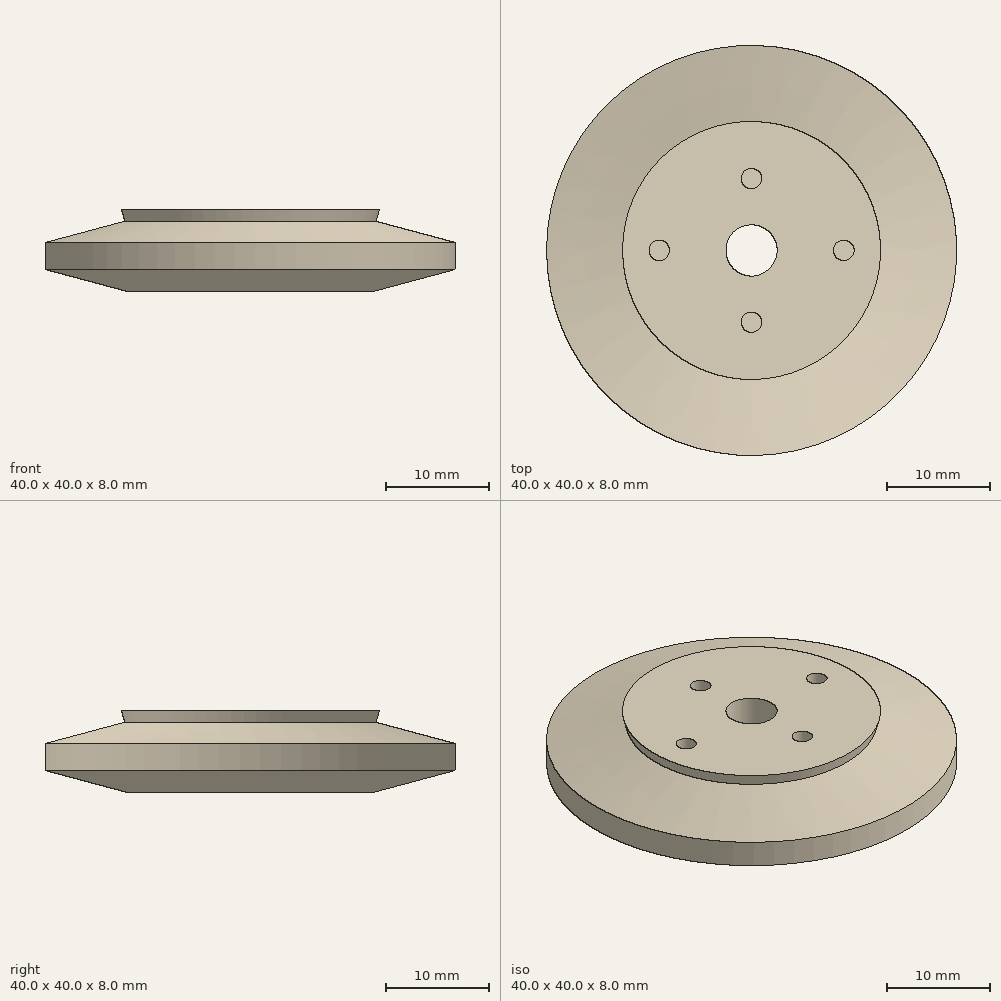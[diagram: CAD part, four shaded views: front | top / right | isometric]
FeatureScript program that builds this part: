
annotation { "Feature Type Name" : "Feature", "Feature Type Description" : "" }
export const myFeature = defineFeature(function(context is Context, id is Id, definition is map)
    precondition{}
    {
        {
            var Q0;
            Q0=qCreatedBy(makeId("Front.planeOp"),FACE);
            var sketch = newSketch(context, id + "F0", { "sketchPlane" : qUnion([Q0])});
            skLineSegment(sketch, "E0", {"start": v(0, 0) * mm, "end": v(20, 0) * mm});
            skLineSegment(sketch, "E1", {"start": v(20, 0) * mm, "end": v(20, 4.77) * mm});
            skLineSegment(sketch, "E2", {"start": v(0, 0) * mm, "end": v(0, 8) * mm});
            skLineSegment(sketch, "E3", {"start": v(0, 8) * mm, "end": v(7.95, 8) * mm});
            skLineSegment(sketch, "E4", {"start": v(20, 4.77) * mm, "end": v(7.95, 8) * mm});
            skLineSegment(sketch, "E5", {"start": v(7.95, 8) * mm, "end": v(12.58, 8) * mm});
            skLineSegment(sketch, "E6", {"start": v(12.27, 6.84) * mm, "end": v(12.58, 8) * mm});
            skLineSegment(sketch, "E7", {"start": v(0, 0) * mm, "end": v(0, 1.6) * mm});
            skLineSegment(sketch, "E8", {"start": v(10, 1.6) * mm, "end": v(0, 1.6) * mm});
            skLineSegment(sketch, "E9", {"start": v(10, 1.6) * mm, "end": v(10, 0) * mm});
            skLineSegment(sketch, "E10", {"start": v(3, 8) * mm, "end": v(3, 0) * mm, "construction": true});
            skLineSegment(sketch, "E11", {"start": v(12, 0) * mm, "end": v(20, 2.14) * mm});
            skLineSegment(sketch, "E12", {"start": v(5, 1.6) * mm, "end": v(5, 0) * mm});
            skSolve(sketch);
        }
        {
            var Q0;
            {var subQ0=sQuery(id+"F0.wireOp",EDGE,"E9");Q0=makeQuery(id+"F0.imprint","IMPRINT",FACE,{"disambiguationData":[TD([[makeQuery(id+"F0.imprint","IMPRINT",EDGE,{"derivedFrom":subQ0}),-1.0]])]});}
            var Q1;
            Q1=sQuery(id+"F0.wireOp",EDGE,"E7");
            revolve(context, id + "F1", {"entities" : qUnion([Q0]), "axis" : qUnion([Q1]), "revolveType" : RevolveType.FULL});
        }
        {
            var Q0;
            {var subQ9=sQuery(id+"F0.wireOp",EDGE,"E9");Q0=makeQuery(id+"F0.imprint","IMPRINT",FACE,{"disambiguationData":[TD([[makeQuery(id+"F0.imprint","IMPRINT",EDGE,{"derivedFrom":subQ9}),1.0]])]});}
            var Q1;
            {var subQ0=sQuery(id+"F0.wireOp",EDGE,"E5");Q1=makeQuery(id+"F0.imprint","IMPRINT",FACE,{"disambiguationData":[TD([[makeQuery(id+"F0.imprint","IMPRINT",EDGE,{"derivedFrom":subQ0}),-1.0]])]});}
            var Q2;
            {var subQ0=sQuery(id+"F0.wireOp",EDGE,"E7");Q2=makeQuery(id+"F0.imprint","IMPRINT",FACE,{"disambiguationData":[TD([[makeQuery(id+"F0.imprint","IMPRINT",EDGE,{"derivedFrom":subQ0}),-1.0]])]});}
            var Q3;
            Q3=sQuery(id+"F0.wireOp",EDGE,"E2");
            revolve(context, id + "F2", {"entities" : qUnion([Q0, Q1, Q2]), "axis" : qUnion([Q3]), "revolveType" : RevolveType.FULL});
        }
        {
            var Q0;
            Q0=makeQuery(id+"F2.opRevolve","SWEPT_FACE",FACE,{"disambiguationData":[OSD([sQuery(id+"F0.wireOp",EDGE,"E3"),sQuery(id+"F0.wireOp",EDGE,"E5")])]});
            var sketch = newSketch(context, id + "F3", { "sketchPlane" : qUnion([Q0])});
            skPoint(sketch, "E13", {"position": v(0, 7) * mm});
            skPoint(sketch, "E14.MirrorP", {"position": v(0, -7) * mm});
            skPoint(sketch, "E15", {"position": v(-9, 0) * mm});
            skPoint(sketch, "E16.MirrorP", {"position": v(9, 0) * mm});
            skPoint(sketch, "E17", {"position": v(0, 0) * mm});
            skSolve(sketch);
        }
        {
            var Q0;
            Q0=sQuery(id+"F3.wireOp",VERTEX,"E15");
            var Q1;
            Q1=sQuery(id+"F3.wireOp",VERTEX,"E13");
            var Q2;
            Q2=sQuery(id+"F3.wireOp",VERTEX,"E16.MirrorP");
            var Q3;
            Q3=sQuery(id+"F3.wireOp",VERTEX,"E14.MirrorP");
            var Q4;
            Q4=makeQuery(id+"F2.opRevolve","SWEPT_BODY",BODY,{"disambiguationData":[OSD([sQuery(id+"F0.wireOp",EDGE,"E0"),sQuery(id+"F0.wireOp",EDGE,"E1"),sQuery(id+"F0.wireOp",EDGE,"E2"),sQuery(id+"F0.wireOp",EDGE,"E3"),sQuery(id+"F0.wireOp",EDGE,"E4"),sQuery(id+"F0.wireOp",EDGE,"E5"),sQuery(id+"F0.wireOp",EDGE,"E6"),sQuery(id+"F0.wireOp",EDGE,"E7"),sQuery(id+"F0.wireOp",EDGE,"E8"),sQuery(id+"F0.wireOp",EDGE,"E9"),sQuery(id+"F0.wireOp",EDGE,"D3B94fJl-vQfu-82kR-nAqz-3uM2DnaGxC46"),sQuery(id+"F0.wireOp",EDGE,"Rp42u3tS-bPXs-FF2L-Fjmg-VZUuCDJLy5qB"),sQuery(id+"F0.wireOp",EDGE,"NfcLsD0d-8hL3-fONj-2pai-6OibrL06urzY"),sQuery(id+"F0.wireOp",EDGE,"ia8oTNWP-idYW-7WVn-FvSA-EXAu2ejEgKzN"),sQuery(id+"F0.wireOp",EDGE,"B5SQBapR-Cnxq-JzNl-lhoH-xMMoOlKLG9fK")])]});
            hole(context, id + "F4", {"style" : HoleStyle.SIMPLE, "endStyle" : HoleEndStyle.THROUGH, "holeDiameter" : 2 * mm, "isTappedThrough" : true, "tappedDepth" : 35 * mm, "tapClearance" : 3, "startFromSketch" : true, "locations" : qUnion([Q0, Q1, Q2, Q3]), "scope" : qUnion([Q4])});
        }
        {
            var Q0;
            Q0=sQuery(id+"F3.wireOp",VERTEX,"E17");
            var Q1;
            Q1=makeQuery(id+"F2.opRevolve","SWEPT_BODY",BODY,{"disambiguationData":[OSD([sQuery(id+"F0.wireOp",EDGE,"E0"),sQuery(id+"F0.wireOp",EDGE,"E1"),sQuery(id+"F0.wireOp",EDGE,"E2"),sQuery(id+"F0.wireOp",EDGE,"E3"),sQuery(id+"F0.wireOp",EDGE,"E4"),sQuery(id+"F0.wireOp",EDGE,"E5"),sQuery(id+"F0.wireOp",EDGE,"E6"),sQuery(id+"F0.wireOp",EDGE,"E8"),sQuery(id+"F0.wireOp",EDGE,"E9"),sQuery(id+"F0.wireOp",EDGE,"E11")])]});
            hole(context, id + "F5", {"style" : HoleStyle.SIMPLE, "endStyle" : HoleEndStyle.THROUGH, "standardTappedOrClearance" : lookupTablePath({ "standard" : "ISO", "engagement" : "75%", "pitch" : "1 mm", "size" : "M6", "type" : "Tapped" }), "standardBlindInLast" : lookupTablePath({ "standard" : "ISO", "engagement" : "75%", "pitch" : "1 mm", "size" : "M6", "type" : "Tapped" }), "holeDiameter" : 5 * mm, "showTappedDepth" : true, "isTappedThrough" : true, "tappedDepth" : 35 * mm, "tapClearance" : 3, "startFromSketch" : true, "locations" : qUnion([Q0]), "scope" : qUnion([Q1]), "majorDiameter" : 6 * mm});
        }
    });
